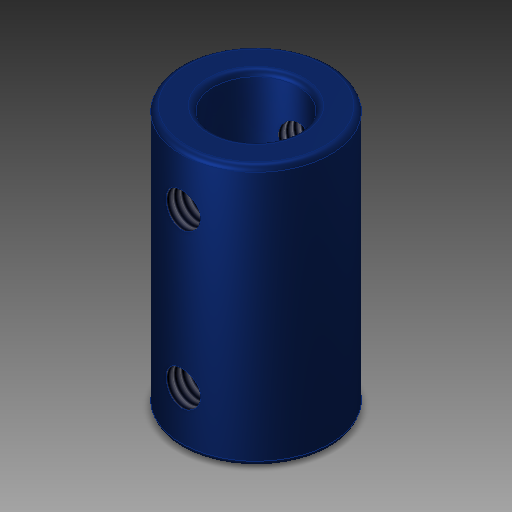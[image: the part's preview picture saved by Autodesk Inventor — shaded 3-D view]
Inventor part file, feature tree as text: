
AUTODESK INVENTOR PART (.ipt)
format: ipt  version: 2017.3 (Build 213256000, 256)  size: 212,992 bytes
history: native  units: mm
features: sketch x4, extrude x3, fillet x1, plane x1, hole x1
ambient origin geometry x8: Origin, YZ Plane, XZ Plane, XY Plane, X Axis, Y Axis, Z Axis, Center Point
bodies: Solid1 (feature_tree)
feature tree (10):
  extrude  "Extrusion1"  Depth=24.5mm TaperAngle=0.0deg
  extrude  "Extrusion2"  Depth=12.25mm TaperAngle=0.0deg
  extrude  "Extrusion3"  Depth=12.25mm TaperAngle=0.0deg
  fillet  "Fillet1"  Radius=0.5mm
  plane  "Work Plane4"
  hole  "Hole3"  [1 undecoded]
  sketch  "Sketch1"  dims[d0=14.0mm d1=24.5mm d2=0.0mm]
  sketch  "Sketch2"  dims[d3=8.0mm d4=12.25mm d5=0.0mm]
  sketch  "Sketch3"  dims[d6=5.0mm d7=12.25mm d8=0.0mm d9=0.5mm]
  sketch  "Sketch8"  dims[d33=3.0mm d34=5.0mm d38=5.0mm d39=3.242mm d40=8.0mm d41=4.0mm d42=2.0mm d43=90.0deg d44=11.8mm d45=20.594885mm]
note: 1 required parameter value undecoded (feature->parameter linkage not recoverable at this tier; creation-order binding heuristic only, values carry confidence <= 0.55)
